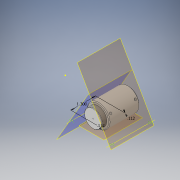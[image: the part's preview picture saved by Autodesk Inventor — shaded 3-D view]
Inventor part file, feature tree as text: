
AUTODESK INVENTOR PART (.ipt)
format: ipt  version: 2019 (Build 230136000, 136)  size: 224,768 bytes
history: native  units: in
note: dims shown in document units (in); Inventor stores cm internally (conversion verified against a paired STEP export)
features: sketch x12, extrude x6, other x3, chamfer x3, plane x3, thread x2, hole x2
ambient origin geometry x8: Origin, YZ Plane, XZ Plane, XY Plane, X Axis, Y Axis, Z Axis, Center Point
bodies: Solid1 (feature_tree)
feature tree (31):
  extrude  "Extrusion1"  Depth=1.6in TaperAngle=0.0deg
  other  "Work Axis1"
  extrude  "Extrusion2"  Depth=0.25in TaperAngle=0.0deg
  chamfer  "Chamfer1"  Distance=0.02in Angle=45.0deg
  chamfer  "Chamfer2"  Distance=0.04in Angle=45.0deg
  thread  "Thread2"  [1 undecoded]
  hole  "Hole1"  [1 undecoded]
  chamfer  "Chamfer3"  Distance=0.3in
  hole  "Hole3"  [1 undecoded]
  extrude  "Extrusion6"  Depth=0.1in
  plane  "Work Plane11"
  sketch  "Sketch12"  dims[d63=0.03in d64=0.3in d65=0.0in]
  sketch  "Sketch19"  dims[d68=0.112in d69=0.112in]
  extrude  "Extrusion9"  Depth=0.4in
  sketch  "Sketch21"  dims[d79=0.1in d80=0.4in]
  sketch  "Sketch22"  dims[d81=1.3in d82=0.35in d83=0.0in]
  plane  "Work Plane17"
  extrude  "Extrusion10"  Depth=0.35in TaperAngle=0.0deg
  plane  "Work Plane18"
  extrude  "Extrusion11"  Depth=0.112in
  thread  "Thread3"  [1 undecoded]
  sketch  "Sketch1"  dims[d0=1.2in d1=1.6in d2=0.0in]
  sketch  "Sketch2"  dims[d3=0.937in d4=0.25in d5=0.0in d6=0.02in d7=0.125in d8=45.0deg d9=0.04in d10=0.125in d11=45.0deg d14=1.0in d15=0.0in]
  sketch  "Sketch4"  dims[d16=0.6in d17=0.5in d18=0.6in d19=0.25in d20=30.0deg d21=1.65in d22=120.0deg d23=0.04in d24=0.125in d25=45.0deg]
  sketch  "Sketch9"  dims[d55=0.03in d56=0.594in d57=0.03in d58=0.25in d59=30.0deg d60=1.65in d61=120.0deg]
  sketch  "Sketch10"  dims[d62=0.03in]
  sketch  "Sketch20"  dims[d71=1.3in d78=0.1in]
  other  "Work Axis10"
  sketch  "Sketch23"  dims[d87=60.0deg d88=0.112in d89=0.112in]
  other  "Work Axis11"
  sketch  "Sketch24"  dims[d90=0.4in d91=1.3in d92=0.35in d93=0.0in d94=60.0deg d95=0.112in d96=0.112in d97=0.4in d98=1.3in d99=0.35in d100=0.0in d101=1.0in d102=0.0in d103=1.0in d104=1.0in d105=1.0in d106=0.15in d107=0.25in d108=0.375in d109=0.5635in d110=0.75in d111=0.8108in d112=0.0625in d113=0.75in d114=0.375in]
note: 4 required parameter values undecoded (feature->parameter linkage not recoverable at this tier; creation-order binding heuristic only, values carry confidence <= 0.55)
